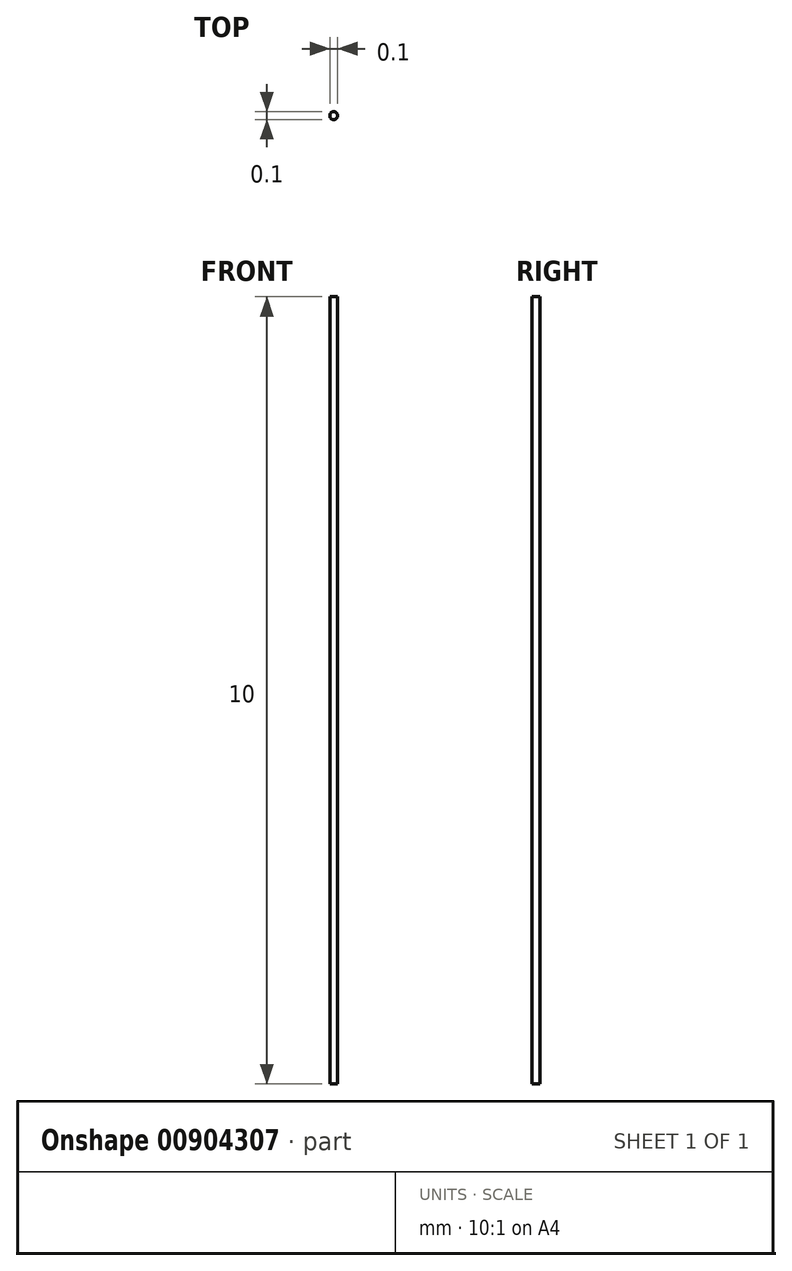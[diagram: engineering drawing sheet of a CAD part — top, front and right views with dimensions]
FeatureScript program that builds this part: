
annotation { "Feature Type Name" : "Feature", "Feature Type Description" : "" }
export const myFeature = defineFeature(function(context is Context, id is Id, definition is map)
    precondition{}
    {
        {
            var Q0;
            Q0=qCreatedBy(makeId("Front.planeOp"),FACE);
            var sketch = newSketch(context, id + "F0", { "sketchPlane" : qUnion([Q0])});
            skLineSegment(sketch, "E0.bottom", {"start": v(0, 0) * mm, "end": v(-0.05, 0) * mm});
            skLineSegment(sketch, "E0.top", {"start": v(0, 10) * mm, "end": v(-0.05, 10) * mm});
            skLineSegment(sketch, "E0.left", {"start": v(0, 0) * mm, "end": v(0, 10) * mm});
            skLineSegment(sketch, "E0.right", {"start": v(-0.05, 0) * mm, "end": v(-0.05, 10) * mm});
            skSolve(sketch);
        }
        {
            var Q0;
            Q0=makeQuery(id+"F0.imprint","IMPRINT",FACE,{"disambiguationData":[TD([[makeQuery(id+"F0.imprint","IMPRINT",EDGE,{"derivedFrom":sQuery(id+"F0.wireOp",EDGE,"E0.bottom")}),-1.0]])]});
            var Q1;
            Q1=sQuery(id+"F0.wireOp",EDGE,"E0.left");
            revolve(context, id + "F1", {"surfaceOperationType" : NewSurfaceOperationType.NEW, "entities" : qUnion([Q0]), "axis" : qUnion([Q1]), "revolveType" : RevolveType.FULL});
        }
    });
